# Revit family: 16. Настенный осевой вентилятор FE Тип А
name_source: partatom
category: Оборудование
revit_build: Autodesk Revit 2016 (Build: 20151209_0715(x64)
units: mm (PartAtom-declared; Revit-internal decimal feet)

## family parameters
Всегда вертикально = Да
На основе рабочей плоскости = Нет
Общий = Нет
При загрузке вырезать с полостями = Нет
Размер круглого соединителя = Использовать диаметр
Тип детали = Нормальный
Точка расчета площади = Нет

## types (4) — shared parameters
R скругления = 15 мм
x = 8 мм
Единица измерения = шт.
Завод изготовитель = KORF
Ключевая пометка = Вентиляция
Материал = Сталь серая
Наименование и тех.хар-ка = Настенный осевой вентилятор
Раздел = ОВ
Размер В = 9 мм
отступ = 32 мм
zero-valued in all types: Мощность, кВт

## per-type parameters (varying)
| type | D | D1 | D2 | d | d1 | d2 | А | Б | Г | Д | Е | Ж | И | Масса единицы | Сила тока J, А | Тип, марка, обозначение | Частота вращения n, об/мин |
| FE031-4DQ | 338 мм | 164 мм | 98 мм | 112 мм | 164 мм | 295 мм | 380 мм | 430 мм | 328 мм | 295 мм | 103 мм | 69 мм | 70 мм | 6,1 кг | 0.29 | FE031-4DQ.OC.A7 | 1410 |
| FE031-4EQ | 338 мм | 164 мм | 98 мм | 112 мм | 164 мм | 295 мм | 380 мм | 430 мм | 328 мм | 295 мм | 103 мм | 69 мм | 70 мм | 6,1 кг | 0.59 | FE031-4EQ.OC.A7 | 1400 |
| FE035-4DQ | 383 мм | 186 мм | 112 мм | 126 мм | 186 мм | 335 мм | 435 мм | 485 мм | 372 мм | 335 мм | 103 мм | 78 мм | 75 мм | 6,9 кг | 0.35 | FE035-4DQ.OC.A7 | 1360 |
| FE035-4EQ | 383 мм | 186 мм | 112 мм | 126 мм | 186 мм | 335 мм | 435 мм | 485 мм | 372 мм | 335 мм | 118 мм | 78 мм | 75 мм | 7.2 кг | 0.9 | FE035-4EQ.OF.A7 | 1400 |
